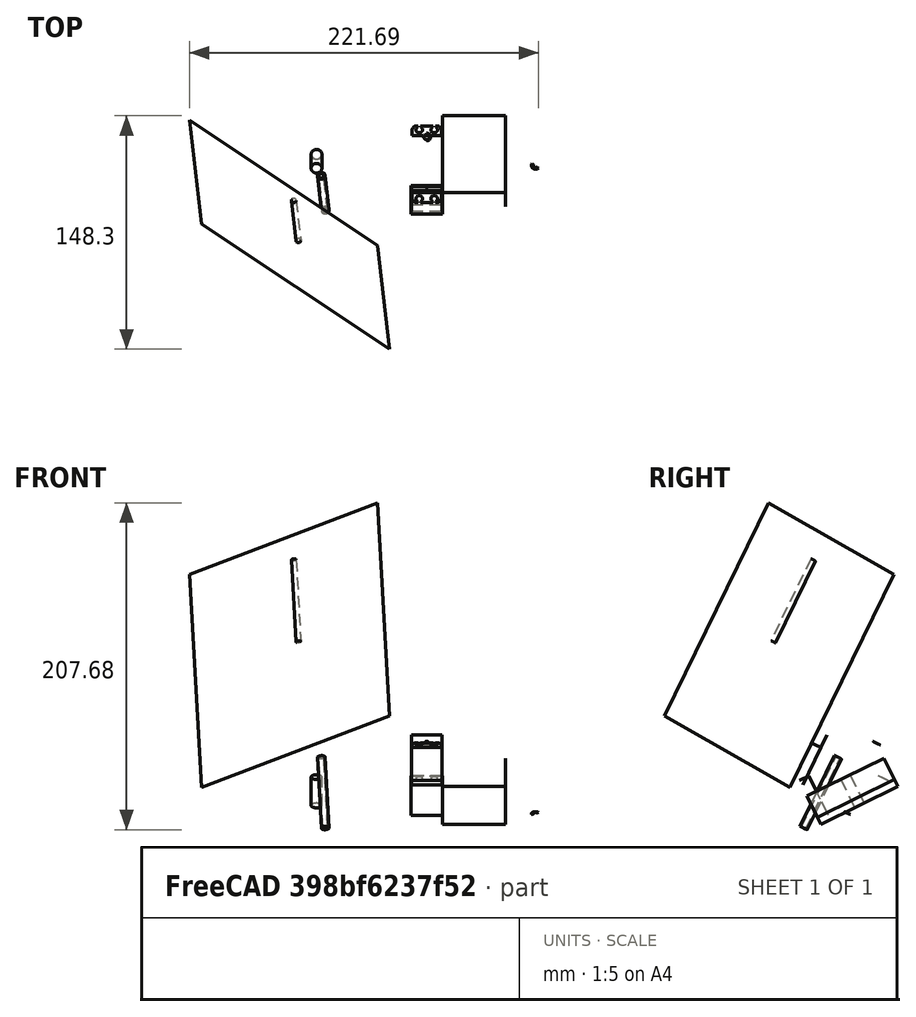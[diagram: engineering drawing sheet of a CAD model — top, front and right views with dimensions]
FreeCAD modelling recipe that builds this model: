
FCSTD DOCUMENT  (FreeCAD 0.19R24366 (Git))
Label: sailface_steerage_assembly_v1
License: All rights reserved
LicenseURL: http://en.wikipedia.org/wiki/All_rights_reserved
objects: App::FeaturePython×20, Part::FeaturePython×17, App::Link×5
note: 16 computed .brp shape members not serialized (recipe doc carries the construction recipe); baked Part::Feature solids carry a one-line shape summary decoded from their .brp
EXTERNAL_REF file=rudder_coarse_1.FCStd obj=Part
EXTERNAL_REF file=ServoSunFinderSF3218MG.FCStd obj=Part002
EXTERNAL_REF file=ServoSunFinderSF3218MG.FCStd obj=Part
EXTERNAL_REF file=ServoSunFinderSF3218MG.FCStd obj=Part001
EXTERNAL_REF file=ServoSunFinderSF3218MG.FCStd obj=Part003

FEATURE [App::Link] Link002  label="PartRudderWithPost"
  LinkPlacement = pos=(-77.119,-40.9847,81.721) rot=(0.845448,-0.472566,-0.248797;1.29098rad)
  LinkedObject = -> <external rudder_coarse_1.FCStd>#Part
  Placement = pos=(-77.119,-40.9847,81.721) rot=(0.845448,-0.472566,-0.248797;1.29098rad)
FEATURE [App::Link] Link003  label="ServoHorn001"
  LinkPlacement = pos=(79.208,1.37065,-28.7732) rot=(-0.078576,0.224256,0.971357;2.48549rad)
  LinkedObject = -> <external ServoSunFinderSF3218MG.FCStd>#Part002
  Placement = pos=(79.208,1.37065,-28.7732) rot=(-0.078576,0.224256,0.971357;2.48549rad)
FEATURE [App::Link] Link004  label="Servo_SF3218MG001"
  LinkPlacement = pos=(0,0,0) rot=(-1,0,0;0.453786rad)
  LinkedObject = -> <external ServoSunFinderSF3218MG.FCStd>#Part
  Placement = pos=(0,0,0) rot=(-1,0,0;0.453786rad)
FEATURE [App::Link] Link005  label="ServoHolderPart"
  LinkPlacement = pos=(0,0,0) rot=(1,0,0;0.456494rad)
  LinkedObject = -> <external ServoSunFinderSF3218MG.FCStd>#Part001
  Placement = pos=(0,0,0) rot=(1,0,0;0.456494rad)
FEATURE [App::Link] Link006  label="PostHoleJacket"
  LinkPlacement = pos=(-54.4606,-25.4419,-34.4738) rot=(-0.993805,-0.11009,0.015223;0.456404rad)
  LinkedObject = -> <external ServoSunFinderSF3218MG.FCStd>#Part003
  Placement = pos=(-54.4606,-25.4419,-34.4738) rot=(-0.993805,-0.11009,0.015223;0.456404rad)
FEATURE [Part::FeaturePython] Parts  # WARN: FeaturePython — macro-defined, semantics opaque (R4)
  Group = -> [Link002,Link003,Link004,Link005,Link006]
  GroupMode = 0
FEATURE [Part::FeaturePython] Assembly  label="SteerageAssembly"  # WARN: FeaturePython — macro-defined, semantics opaque (R4)
  AutoRelax = true
  BuildShape = 0
  Freeze = false
  Group = -> [Constraints,Elements,Parts,Relations]
  Verbose = false
  _SolverType = 1
  _Version = 1
FEATURE [App::FeaturePython] Constraints  # WARN: FeaturePython — macro-defined, semantics opaque (R4)
  Group = -> [Constraint001,Constraint002,Constraint,Constraint004]
  _Version = 1
FEATURE [App::FeaturePython] Elements  # WARN: FeaturePython — macro-defined, semantics opaque (R4)
  Group = -> [_Element,_Element002,_Element003,_Element004,_Element005,_Element008,_Element022,_Element024,Element,Element001,Element002,_Element025,_Element026,_Element027,_Element028]
FEATURE [Part::FeaturePython] _Element  # link proxy (typed FeaturePython)
  Detach = false
  LinkTransform = true
  LinkedObject = -> Link002 [Extrude001.Face1]
  _Parent = -> Elements
FEATURE [Part::FeaturePython] _Element002  # link proxy (typed FeaturePython)
  Detach = false
  LinkTransform = true
  LinkedObject = -> Link004 [Solid.Face66]
  _Parent = -> Elements
FEATURE [Part::FeaturePython] _Element003  # link proxy (typed FeaturePython)
  Detach = false
  LinkTransform = true
  LinkedObject = -> Link003 [Solid001.Face34]
  _Parent = -> Elements
FEATURE [App::FeaturePython] Constraint001  label="PlaneCoincident"  # WARN: FeaturePython — macro-defined, semantics opaque (R4)
  Angle = 0
  AnglePitch = 0
  AngleRoll = 0
  Cascade = false
  Disabled = true
  Group = -> [ElementLink002,ElementLink003]
  LockAngle = false
  Multiply = false
  OffsetX = 0
  OffsetY = 0
  _ConstraintType = 35
  _Parent = -> Constraints
FEATURE [App::FeaturePython] ElementLink002  label="_Element002"  # link proxy (typed FeaturePython)
  LinkTransform = true
  LinkedObject = -> _Element002
  _Parent = -> Constraint001
FEATURE [App::FeaturePython] ElementLink003  label="_Element003"  # link proxy (typed FeaturePython)
  LinkTransform = true
  LinkedObject = -> _Element003
  _Parent = -> Constraint001
FEATURE [App::FeaturePython] Constraint002  label="AxialAlignment001"  # WARN: FeaturePython — macro-defined, semantics opaque (R4)
  Angle = 0
  AnglePitch = 0
  AngleRoll = 0
  Disabled = true
  Group = -> [ElementLink004,ElementLink005]
  LockAngle = false
  Multiply = false
  _ConstraintType = 36
  _Parent = -> Constraints
FEATURE [App::FeaturePython] ElementLink004  label="_Element004"  # link proxy (typed FeaturePython)
  LinkTransform = true
  LinkedObject = -> _Element004
  _Parent = -> Constraint002
FEATURE [Part::FeaturePython] _Element004  # link proxy (typed FeaturePython)
  Detach = false
  LinkTransform = true
  LinkedObject = -> Link006 [Body002.Pocket003.Face4]
  _Parent = -> Elements
FEATURE [App::FeaturePython] ElementLink005  label="_Element"  # link proxy (typed FeaturePython)
  LinkTransform = true
  LinkedObject = -> _Element
  _Parent = -> Constraint002
FEATURE [Part::FeaturePython] _Element005  # link proxy (typed FeaturePython)
  Detach = false
  LinkTransform = true
  LinkedObject = -> Link004 [Solid.Face27]
  _Parent = -> Elements
FEATURE [Part::FeaturePython] _Element008  # link proxy (typed FeaturePython)
  Detach = false
  LinkTransform = true
  LinkedObject = -> Link004 [Solid.Face33]
  _Parent = -> Elements
FEATURE [Part::FeaturePython] _Element022  # link proxy (typed FeaturePython)
  Detach = false
  LinkTransform = true
  LinkedObject = -> Link006 [Body002.Pocket003.Face1]
  _Parent = -> Elements
FEATURE [Part::FeaturePython] _Element024  label="YZ_Plane@PartRudderWithPost"  # link proxy (typed FeaturePython)
  Detach = false
  LinkTransform = true
  LinkedObject = -> Link002 [Origin.YZ_Plane.]
  _Parent = -> Elements
FEATURE [Part::FeaturePython] Element  # link proxy (typed FeaturePython)
  Detach = false
  LinkTransform = true
  LinkedObject = -> Link005 [Body001.Pad010.Face42]
  _Parent = -> Elements
FEATURE [Part::FeaturePython] Element001  # link proxy (typed FeaturePython)
  Detach = false
  LinkTransform = true
  LinkedObject = -> Link005 [Body001.Pad010.Face36]
  _Parent = -> Elements
FEATURE [Part::FeaturePython] Element002  # link proxy (typed FeaturePython)
  Detach = false
  LinkTransform = true
  LinkedObject = -> Link005 [Body001.Pad010.Face39]
  _Parent = -> Elements
FEATURE [App::FeaturePython] Constraint  label="AxialAlignment"  # WARN: FeaturePython — macro-defined, semantics opaque (R4)
  Angle = 0
  AnglePitch = 0
  AngleRoll = 0
  Disabled = true
  Group = -> [ElementLink,ElementLink006]
  LockAngle = false
  Multiply = false
  _ConstraintType = 36
  _Parent = -> Constraints
FEATURE [App::FeaturePython] ElementLink  label="_Element022"  # link proxy (typed FeaturePython)
  LinkTransform = true
  LinkedObject = -> _Element022
  _Parent = -> Constraint
FEATURE [App::FeaturePython] ElementLink006  label="_Element025"  # link proxy (typed FeaturePython)
  LinkTransform = true
  LinkedObject = -> _Element025
  _Parent = -> Constraint
FEATURE [Part::FeaturePython] _Element025  # link proxy (typed FeaturePython)
  Detach = false
  LinkTransform = true
  LinkedObject = -> Link005 [Body001.Pad010.Face6]
  _Parent = -> Elements
FEATURE [Part::FeaturePython] _Element026  # link proxy (typed FeaturePython)
  Detach = false
  LinkTransform = true
  LinkedObject = -> Link004 [Solid.Face107]
  _Parent = -> Elements
FEATURE [Part::FeaturePython] _Element027  # link proxy (typed FeaturePython)
  Detach = false
  LinkTransform = true
  LinkedObject = -> Link005 [Body001.Pad010.Face23]
  _Parent = -> Elements
FEATURE [App::FeaturePython] Constraint004  label="PlaneCoincident001"  # WARN: FeaturePython — macro-defined, semantics opaque (R4)
  Angle = 0
  AnglePitch = 0
  AngleRoll = 0
  Cascade = false
  Disabled = true
  Group = -> [ElementLink009,ElementLink010]
  LockAngle = false
  Multiply = false
  OffsetX = 0
  OffsetY = 0
  _ConstraintType = 35
  _Parent = -> Constraints
FEATURE [App::FeaturePython] ElementLink009  label="_Element028"  # link proxy (typed FeaturePython)
  LinkTransform = true
  LinkedObject = -> _Element028
  _Parent = -> Constraint004
FEATURE [Part::FeaturePython] _Element028  # link proxy (typed FeaturePython)
  Detach = false
  LinkTransform = true
  LinkedObject = -> Link005 [Body001.Pad010.Face21]
  _Parent = -> Elements
FEATURE [App::FeaturePython] ElementLink010  label="_Element008"  # link proxy (typed FeaturePython)
  LinkTransform = true
  LinkedObject = -> _Element008
  _Parent = -> Constraint004
FEATURE [App::FeaturePython] Relations  # WARN: FeaturePython — macro-defined, semantics opaque (R4)
  Constraints = -> Constraints
  Group = -> [Relation,Relation001,Relation002,Relation003,Relation004]
FEATURE [App::FeaturePython] Relation  label="PartRudderWithPost"  # WARN: FeaturePython — macro-defined, semantics opaque (R4)
  Count = 0
  Group = -> [Constraint002]
  Index = 0
  Part = -> Link002
FEATURE [App::FeaturePython] Relation001  label="ServoHorn001"  # WARN: FeaturePython — macro-defined, semantics opaque (R4)
  Count = 0
  Group = -> [Constraint001]
  Index = 0
  Part = -> Link003
FEATURE [App::FeaturePython] Relation002  label="Servo_SF3218MG001"  # WARN: FeaturePython — macro-defined, semantics opaque (R4)
  Count = 0
  Group = -> [Constraint001,Constraint004]
  Index = 0
  Part = -> Link004
FEATURE [App::FeaturePython] Relation003  label="ServoHolderPart"  # WARN: FeaturePython — macro-defined, semantics opaque (R4)
  Count = 0
  Group = -> [Constraint,Constraint004]
  Index = 0
  Part = -> Link005
FEATURE [App::FeaturePython] Relation004  label="PostHoleJacket"  # WARN: FeaturePython — macro-defined, semantics opaque (R4)
  Count = 0
  Group = -> [Constraint002,Constraint]
  Index = 0
  Part = -> Link006

RESOLVED EXTERNAL PARTS (link-assembly join: the EXTERNAL_REF files above that resolve inside this repo's crawl, each included once):
---- part rudder_coarse_1.FCStd = doc fcstd_55b8d1ebdd48 ----
FCSTD DOCUMENT  (FreeCAD 0.19R24366 (Git))
Label: rudder_coarse_1
License: All rights reserved
LicenseURL: http://en.wikipedia.org/wiki/All_rights_reserved
objects: Sketcher::SketchObject×6, Part::Extrusion×5, App::Part×3, Image::ImagePlane×2, PartDesign::FeatureBase×1, PartDesign::Body×1
note: 13 computed .brp shape members not serialized (recipe doc carries the construction recipe); baked Part::Feature solids carry a one-line shape summary decoded from their .brp

FEATURE [Image::ImagePlane] ImagePlane  label="RudderSourceImagePlane"
  XSize = 140.897
  YSize = 140.897
FEATURE [Sketcher::SketchObject] Sketch
  FullyConstrained = false
  MapMode = 2
  Support = -> [ImagePlane]
  sketch-geometry (4):
    g0: LineSegment StartX=-21.1422 StartY=-0.0475752 StartZ=0 EndX=16.8578 EndY=-0.0475752 EndZ=0
    g1: LineSegment StartX=16.8578 StartY=-0.0475752 StartZ=0 EndX=16.8578 EndY=-52.0476 EndZ=0
    g2: LineSegment StartX=16.8578 StartY=-52.0476 StartZ=0 EndX=-12.1422 EndY=-48.0476 EndZ=0
    g3: LineSegment StartX=-12.1422 StartY=-48.0476 StartZ=0 EndX=-21.1422 EndY=-0.0475752 EndZ=0
  constraints (10):
    c: Horizontal(g0)
    c: Coincident(g1,g0)
    c: Vertical(g1)
    c: Coincident(g3,g0)
    c: DistanceX(g2,g1) = 29
    c: Coincident(g2,g3)
    c: Coincident(g2,g1)
    c: DistanceY(g1,g0) = 52
    c: DistanceY(g2,g0) = 48
    c: DistanceX(g0,g0) = 38
FEATURE [Part::Extrusion] Extrude  label="RudderExtrude"
  Base = -> Sketch
  Dir = (0,0,1)
  DirLink = -> XY_Plane
  DirMode = 2
  FaceMakerClass = Part::FaceMakerBullseye
  LengthFwd = 5
  LengthRev = 0
  Solid = true
  Symmetric = true
FEATURE [Sketcher::SketchObject] Sketch001
  FullyConstrained = false
  MapMode = 5
  Placement = pos=(0,-0.0475752,0) rot=(0,0.707107,0.707107;3.14159rad)
  Support = -> [Extrude]
  sketch-geometry (1):
    g0: Circle CenterX=-7.11491 CenterY=0 CenterZ=0 NormalX=0 NormalY=0 NormalZ=1 AngleXU=0 Radius=1.5
  constraints (2):
    c: Radius(g0) = 1.5
    c: PointOnObject(g0,g-1)
FEATURE [Part::Extrusion] Extrude001  label="PostExtrude"
  Base = -> Sketch001
  Dir = (0,-1,0)
  DirMode = 0
  FaceMakerClass = Part::FaceMakerBullseye
  LengthFwd = -58
  LengthRev = 0
  Solid = true
  Symmetric = false
FEATURE [App::Part] Part  label="PartRudderWithPost"
  Group = -> [Extrude,Sketch001,Extrude001,Sketch]
  Origin = -> Origin
FEATURE [Sketcher::SketchObject] Sketch014
  FullyConstrained = false
  Placement = pos=(45.664,-0.0649673,72.7031) rot=(-0.007022,-0.001094,0.999975;1.56956rad)
  sketch-geometry (1):
    g0: Circle CenterX=0 CenterY=191.792 CenterZ=0 NormalX=0 NormalY=0 NormalZ=1 AngleXU=0 Radius=2.5
  constraints (2):
    c: PointOnObject(g0,g-2)
    c: Radius(g0) = 2.5
FEATURE [Part::Extrusion] Extrude002
  Base = -> Sketch014
  Dir = (0,0,1)
  DirMode = 0
  FaceMakerClass = Part::FaceMakerBullseye
  LengthFwd = 48
  LengthRev = 0
  Solid = true
  Symmetric = true
FEATURE [Image::ImagePlane] ImagePlane001  label="RudderConnector"
  Placement = pos=(-2.35,0,2.6) rot=(-1,0,0;4.71239rad)
  XSize = 57.8573
  YSize = 57.8573
FEATURE [Sketcher::SketchObject] Sketch018
  FullyConstrained = false
  Placement = pos=(0,0,0) rot=(1,0,0;1.5708rad)
  sketch-geometry (13):
    g0: LineSegment StartX=-18.3077 StartY=2.40747 StartZ=0 EndX=-6.02783 EndY=4.31937 EndZ=0
    g1: LineSegment StartX=-3.97641 StartY=6.22764 StartZ=0 EndX=-1.18261 EndY=18.3382 EndZ=0
    g2: LineSegment StartX=2.74256 StartY=18.1953 StartZ=0 EndX=5.43496 EndY=0.843309 EndZ=0
    g3: LineSegment StartX=-1.19806 StartY=-5.36793 StartZ=0 EndX=-18.4357 EndY=-1.5207 EndZ=0
    g4: ArcOfCircle CenterX=-18 CenterY=0.431279 CenterZ=0 NormalX=0 NormalY=0 NormalZ=1 AngleXU=0 Radius=2 StartAngle=1.72525 EndAngle=4.4928
    g5: ArcOfCircle CenterX=0 CenterY=0 CenterZ=0 NormalX=0 NormalY=0 NormalZ=1 AngleXU=0 Radius=5.5 StartAngle=4.4928 EndAngle=6.43712
    g6: ArcOfCircle CenterX=0.766208 CenterY=17.8887 CenterZ=0 NormalX=0 NormalY=0 NormalZ=1 AngleXU=0 Radius=2 StartAngle=0.153936 EndAngle=2.91487
    g7: Circle CenterX=0 CenterY=0 CenterZ=0 NormalX=0 NormalY=0 NormalZ=1 AngleXU=0 Radius=1.5
    g8: Circle CenterX=-18 CenterY=0.431279 CenterZ=0 NormalX=0 NormalY=0 NormalZ=1 AngleXU=0 Radius=1
    g9: Circle CenterX=-14 CenterY=0.275124 CenterZ=0 NormalX=0 NormalY=0 NormalZ=1 AngleXU=0 Radius=1.02606
    g10: Circle CenterX=0.766208 CenterY=17.8887 CenterZ=0 NormalX=0 NormalY=0 NormalZ=1 AngleXU=0 Radius=1
    g11: Circle CenterX=0.585844 CenterY=13.8887 CenterZ=0 NormalX=0 NormalY=0 NormalZ=1 AngleXU=0 Radius=1
    g12: ArcOfCircle CenterX=-6.41243 CenterY=6.7896 CenterZ=0 NormalX=0 NormalY=0 NormalZ=1 AngleXU=0 Radius=2.5 StartAngle=4.86684 EndAngle=6.05646
  constraints (23):
    c: DistanceX(g4,g5) = 18
    c: Coincident(g7,g5)
    c: Radius(g7) = 1.5
    c: Coincident(g8,g4)
    c: Coincident(g10,g6)
    c: Radius(g8) = 1
    c: DistanceX(g9,g5) = 14
    c: Tangent(g5,g3) = 1.5708
    c: Tangent(g4,g3) = 1.5708
    c: Tangent(g5,g2) = 1.5708
    c: Radius(g5) = 5.5
    c: Tangent(g6,g1) = 1.5708
    c: Tangent(g6,g2) = 1.5708
    c: Radius(g10) = 1
    c: Tangent(g0,g12) = -1.5708
    c: Tangent(g1,g12) = -1.5708
    c: Radius(g11) = 1
    c: Radius(g6) = 2
    c: DistanceY(g11,g6) = 4
    c: Radius(g4) = 2
    c: Coincident(g-1,g5)
    c: Tangent(g4,g0) = 1.5708
    c: Radius(g12) = 2.5
FEATURE [Part::Extrusion] Extrude005
  Base = -> Sketch018
  Dir = (0,1,0)
  DirMode = 0
  FaceMakerClass = Part::FaceMakerBullseye
  LengthFwd = 3
  LengthRev = 0
  Solid = true
  Symmetric = false
FEATURE [Sketcher::SketchObject] Sketch017
  FullyConstrained = true
  MapMode = 5
  Placement = pos=(0,0,0) rot=(1,0,0;1.5708rad)
  Support = -> [Extrude005]
  sketch-geometry (2):
    g0: Circle CenterX=0 CenterY=0 CenterZ=0 NormalX=0 NormalY=0 NormalZ=1 AngleXU=0 Radius=5.5
    g1: Circle CenterX=0 CenterY=0 CenterZ=0 NormalX=0 NormalY=0 NormalZ=1 AngleXU=0 Radius=1.5
  constraints (4):
    c: Coincident(g0,g-1)
    c: Coincident(g1,g0)
    c: Radius(g1) = 1.5
    c: Radius(g0) = 5.5
FEATURE [Part::Extrusion] Extrude006
  Base = -> Sketch017
  Dir = (0,1,0)
  DirMode = 0
  FaceMakerClass = Part::FaceMakerBullseye
  LengthFwd = -1
  LengthRev = 0
  Solid = true
  Symmetric = false
FEATURE [App::Part] Part002  label="PartRudderConnector"
  Group = -> [Sketch018,Extrude006,Sketch017,Extrude005]
  Origin = -> Origin002
FEATURE [Sketcher::SketchObject] Sketch019
  ExternalGeometry = -> [Extrude002]
  FullyConstrained = true
  MapMode = 5
  Placement = pos=(-0.780985,0.571169,96.3228) rot=(-0.590327,-0.807161,0.002393;0.010045rad)
  Support = -> [Extrude002]
  sketch-geometry (1):
    g0: Circle CenterX=-145.346 CenterY=-0.391104 CenterZ=0 NormalX=0 NormalY=0 NormalZ=1 AngleXU=0 Radius=1.5
  constraints (3):
    c: Diameter(g0) = 3
    c: Coincident(g0,g-3)
    c: Diameter(g-3) = 5
FEATURE [PartDesign::FeatureBase] BaseFeature
  BaseFeature = -> Extrude002
FEATURE [PartDesign::Body] Body  label="PostHoleJacketBody"
  BaseFeature = -> Extrude002
  Group = -> [BaseFeature,Sketch019]
  Origin = -> Origin003
  Tip = -> BaseFeature
FEATURE [App::Part] Part001  label="PostHoleJacket"
  Group = -> [Body]
  Origin = -> Origin001
